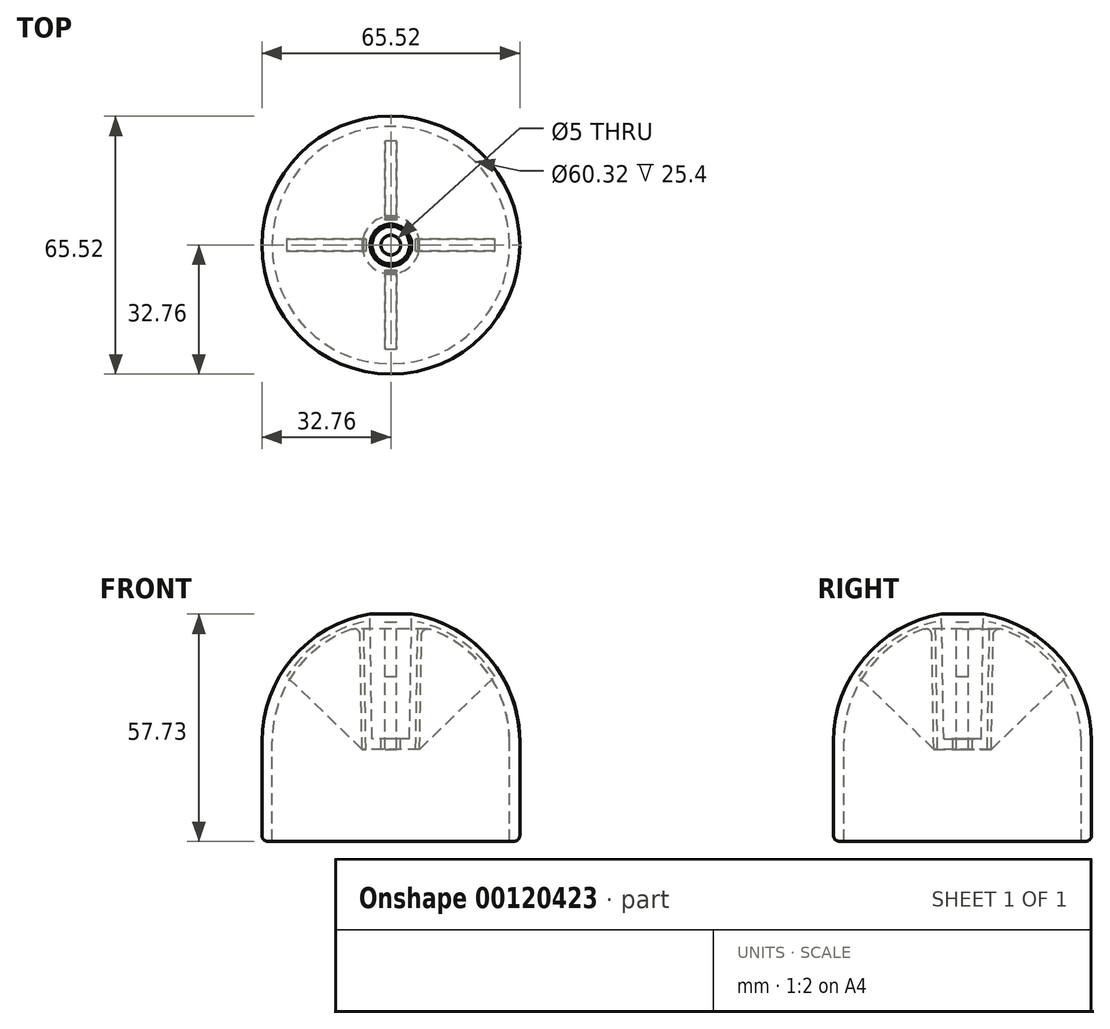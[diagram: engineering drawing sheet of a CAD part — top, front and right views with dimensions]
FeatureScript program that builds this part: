
annotation { "Feature Type Name" : "Feature", "Feature Type Description" : "" }
export const myFeature = defineFeature(function(context is Context, id is Id, definition is map)
    precondition{}
    {
        {
            var Q0;
            Q0=qCreatedBy(makeId("Front.planeOp"),FACE);
            var sketch = newSketch(context, id + "F0", { "sketchPlane" : qUnion([Q0])});
            skLineSegment(sketch, "E0", {"start": v(-30.16, 0) * mm, "end": v(30.16, 0) * mm, "construction": true});
            skLineSegment(sketch, "E1", {"start": v(30.16, 0) * mm, "end": v(32.76, 0) * mm});
            skLineSegment(sketch, "E2", {"start": v(30.16, 0) * mm, "end": v(30.16, 25.4) * mm});
            skArc(sketch, "E3", {"start": v(30.16, 25.4) * mm, "mid": v(23.95, 43.74) * mm, "end": v(7.86, 54.52) * mm});
            skLineSegment(sketch, "E4", {"start": v(0, 55.56) * mm, "end": v(-23.74, 55.56) * mm, "construction": true});
            skArc(sketch, "E5", {"start": v(7.86, 54.52) * mm, "mid": v(3.96, 55.3) * mm, "end": v(0, 55.56) * mm, "construction": true});
            skLineSegment(sketch, "E6", {"start": v(7.86, 54.52) * mm, "end": v(7.32, 23.38) * mm});
            skLineSegment(sketch, "E7", {"start": v(7.32, 23.38) * mm, "end": v(2.5, 23.38) * mm});
            skLineSegment(sketch, "E8.0", {"start": v(4.76, 25.98) * mm, "end": v(2.5, 25.98) * mm});
            skLineSegment(sketch, "E8.1", {"start": v(5.32, 57.73) * mm, "end": v(4.76, 25.98) * mm});
            skArc(sketch, "E8.2", {"start": v(32.76, 25.4) * mm, "mid": v(24.98, 46.6) * mm, "end": v(5.32, 57.73) * mm});
            skLineSegment(sketch, "E8.3", {"start": v(32.76, 0) * mm, "end": v(32.76, 25.4) * mm});
            skLineSegment(sketch, "E9", {"start": v(2.5, 25.98) * mm, "end": v(2.5, 23.38) * mm});
            skLineSegment(sketch, "E10", {"start": v(4.76, 25.98) * mm, "end": v(-4.76, 25.98) * mm, "construction": true});
            skLineSegment(sketch, "E11", {"start": v(0, 25.98) * mm, "end": v(0, 0) * mm, "construction": true});
            skSolve(sketch);
        }
        {
            var Q0;
            Q0=makeQuery(id+"F0.imprint","IMPRINT",FACE,{"disambiguationData":[TD([[makeQuery(id+"F0.imprint","IMPRINT",EDGE,{"derivedFrom":sQuery(id+"F0.wireOp",EDGE,"E1")}),1.0]])]});
            var Q1;
            Q1=sQuery(id+"F0.wireOp",EDGE,"E11");
            revolve(context, id + "F1", {"entities" : qUnion([Q0]), "axis" : qUnion([Q1]), "revolveType" : RevolveType.FULL});
        }
        {
            var Q0;
            Q0=makeQuery(id+"F1.opRevolve","SWEPT_EDGE",EDGE,{"disambiguationData":[OSD([sQuery(id+"F0.wireOp",EDGE,"E1"),sQuery(id+"F0.wireOp",EDGE,"E8.3")])]});
            fillet(context, id + "F2", {"entities" : qUnion([Q0]), "radius" : 1.5 * mm, "tangentPropagation" : true, "allowEdgeOverflow" : false});
        }
        {
            var Q0;
            Q0=qCreatedBy(makeId("Front.planeOp"),FACE);
            var sketch = newSketch(context, id + "F3", { "sketchPlane" : qUnion([Q0])});
            skArc(sketch, "E12", {"start": v(7.86, 54.52) * mm, "mid": v(23.95, 43.74) * mm, "end": v(30.16, 25.4) * mm, "construction": true});
            skLineSegment(sketch, "E13", {"start": v(30.16, 25.4) * mm, "end": v(30.16, 0) * mm, "construction": true});
            skLineSegment(sketch, "E14", {"start": v(7.32, 23.38) * mm, "end": v(7.86, 54.52) * mm, "construction": true});
            skLineSegment(sketch, "E15", {"start": v(7.32, 23.38) * mm, "end": v(6.32, 23.4) * mm});
            skLineSegment(sketch, "E16", {"start": v(6.32, 23.4) * mm, "end": v(6.88, 55.8) * mm});
            skArc(sketch, "E17.1", {"start": v(6.88, 55.8) * mm, "mid": v(18.07, 50.8) * mm, "end": v(26.46, 41.86) * mm});
            skLineSegment(sketch, "E18", {"start": v(7.32, 23.38) * mm, "end": v(26.46, 41.86) * mm});
            skSolve(sketch);
        }
        {
            var Q0;
            Q0=qSketchRegion(id+"F3",true);
            extrude(context, id + "F4", {"entities" : qUnion([Q0]), "endBound" : BoundingType.SYMMETRIC, "depth" : 3 * mm});
        }
        {
            var Q0;
            Q0=makeQuery(id+"F4.opExtrude","SWEPT_BODY",BODY,{"disambiguationData":[OSD([sQuery(id+"F3.wireOp",EDGE,"E15"),sQuery(id+"F3.wireOp",EDGE,"E16"),sQuery(id+"F3.wireOp",EDGE,"E17.1"),sQuery(id+"F3.wireOp",EDGE,"E18")])]});
            var Q1;
            Q1=sQuery(id+"F0.wireOp",EDGE,"E11");
            circularPattern(context, id + "F5", {"entities" : qUnion([Q0]), "axis" : qUnion([Q1]), "angle" : 360 * degree, "instanceCount" : 4, "equalSpace" : true});
        }
        {
            var Q0;
            Q0=makeQuery(id+"F1.opRevolve","SWEPT_FACE",FACE,{"disambiguationData":[OSD([sQuery(id+"F0.wireOp",EDGE,"E3")])]});
            fillet(context, id + "F6", {"entities" : qUnion([Q0]), "radius" : 1.5 * mm, "tangentPropagation" : true, "allowEdgeOverflow" : false});
        }
    });
